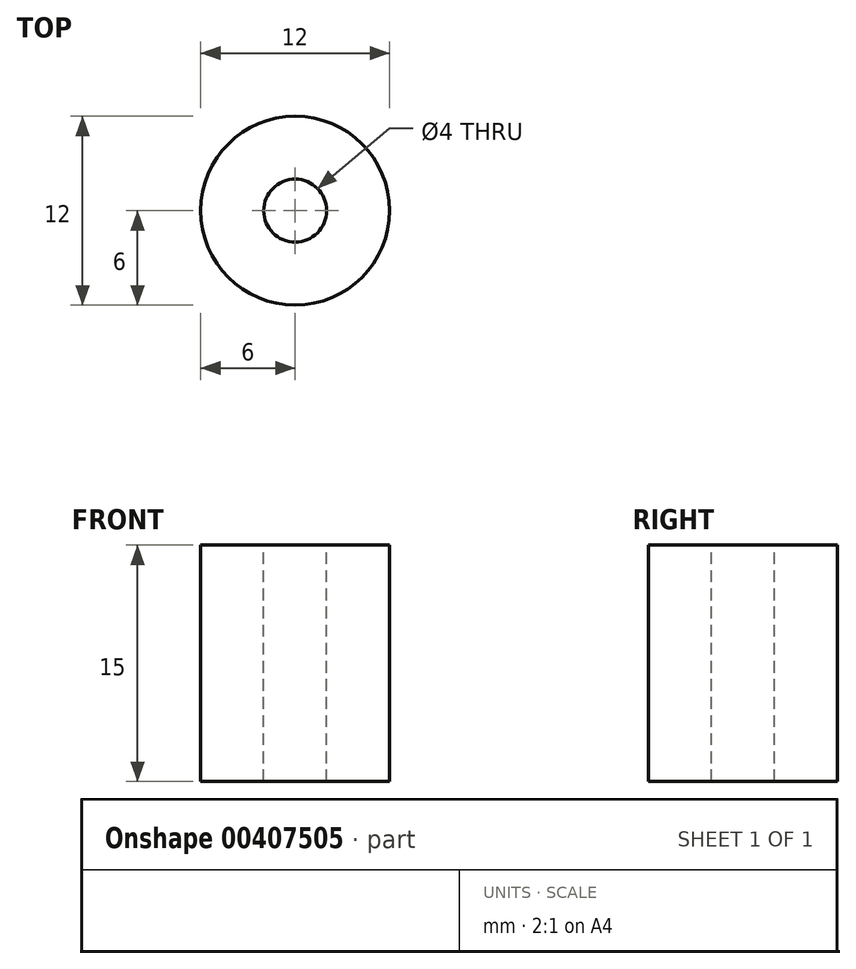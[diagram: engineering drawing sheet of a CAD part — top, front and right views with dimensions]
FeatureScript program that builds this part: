
annotation { "Feature Type Name" : "Feature", "Feature Type Description" : "" }
export const myFeature = defineFeature(function(context is Context, id is Id, definition is map)
    precondition{}
    {
        {
            var Q0;
            Q0=qCreatedBy(makeId("Top.planeOp"),FACE);
            var sketch = newSketch(context, id + "F0", { "sketchPlane" : qUnion([Q0])});
            skCircle(sketch, "E0", {"center": v(0, 0) * mm, "radius": 6 * mm});
            skSolve(sketch);
        }
        {
            var Q0;
            Q0=makeQuery(id+"F0.imprint","IMPRINT",FACE,{"disambiguationData":[TD([[makeQuery(id+"F0.imprint","IMPRINT",EDGE,{"derivedFrom":sQuery(id+"F0.wireOp",EDGE,"E0")}),1.0]])]});
            extrude(context, id + "F1", {"entities" : qUnion([Q0]), "depth" : 15 * mm, "offsetDistance" : 25 * mm});
        }
        {
            var Q0;
            Q0=makeQuery(id+"F1.opExtrude","CAP_FACE",FACE,{"disambiguationData":[OSD([sQuery(id+"F0.wireOp",EDGE,"E0")])],"isStart":false});
            var sketch = newSketch(context, id + "F2", { "sketchPlane" : qUnion([Q0])});
            skCircle(sketch, "E1", {"center": v(0, 0) * mm, "radius": 2 * mm});
            skSolve(sketch);
        }
        {
            var Q0;
            Q0=makeQuery(id+"F2.imprint","IMPRINT",FACE,{"disambiguationData":[TD([[makeQuery(id+"F2.imprint","IMPRINT",EDGE,{"derivedFrom":sQuery(id+"F2.wireOp",EDGE,"E1")}),1.0]])]});
            extrude(context, id + "F3", {"entities" : qUnion([Q0]), "operationType" : NewBodyOperationType.REMOVE, "endBound" : BoundingType.THROUGH_ALL, "oppositeDirection" : true, "depth" : 3 * mm});
        }
    });
